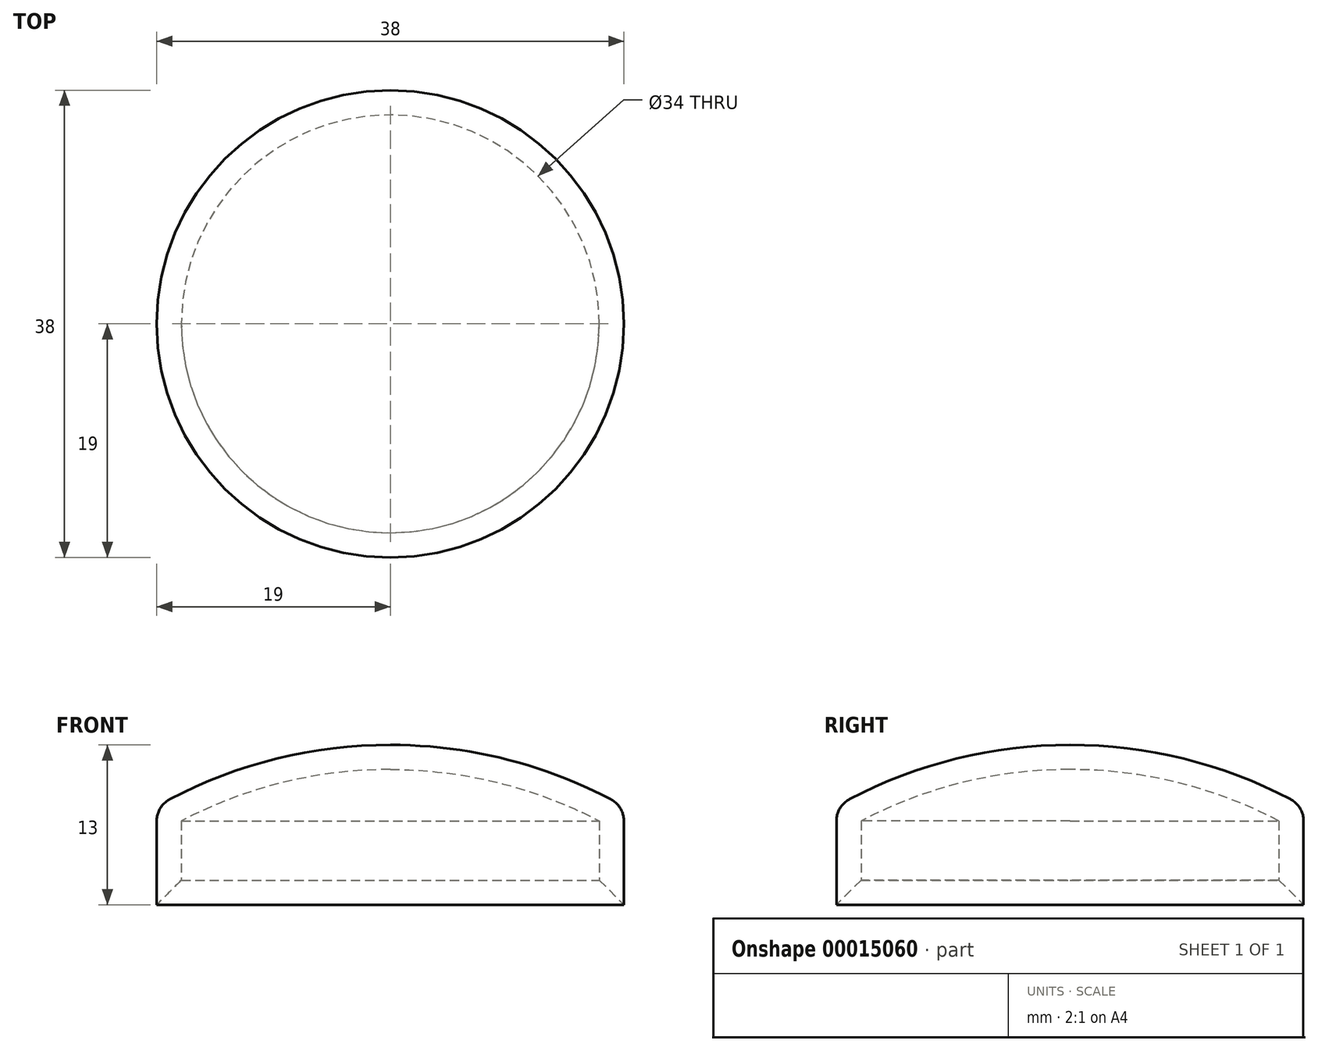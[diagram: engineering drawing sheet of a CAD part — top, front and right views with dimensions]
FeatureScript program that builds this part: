
annotation { "Feature Type Name" : "Feature", "Feature Type Description" : "" }
export const myFeature = defineFeature(function(context is Context, id is Id, definition is map)
    precondition{}
    {
        {
            var Q0;
            Q0=qCreatedBy(makeId("Front.planeOp"),FACE);
            var sketch = newSketch(context, id + "F0", { "sketchPlane" : qUnion([Q0])});
            skLineSegment(sketch, "E0", {"start": v(0, 0) * mm, "end": v(0, 25.64) * mm, "construction": true});
            skLineSegment(sketch, "E1", {"start": v(0, 0) * mm, "end": v(23.76, 0) * mm, "construction": true});
            skLineSegment(sketch, "E2.bottom", {"start": v(0, 0) * mm, "end": v(19, 0) * mm});
            skLineSegment(sketch, "E2.top", {"start": v(0, 8) * mm, "end": v(19, 8) * mm, "construction": true});
            skLineSegment(sketch, "E2.left", {"start": v(0, 0) * mm, "end": v(0, 8) * mm});
            skLineSegment(sketch, "E2.right", {"start": v(19, 0) * mm, "end": v(19, 6.81) * mm});
            skLineSegment(sketch, "E3.top", {"start": v(0, 13) * mm, "end": v(19, 13) * mm, "construction": true});
            skLineSegment(sketch, "E3.left", {"start": v(0, 8) * mm, "end": v(0, 13) * mm});
            skLineSegment(sketch, "E3.right", {"start": v(19, 8) * mm, "end": v(19, 13) * mm, "construction": true});
            skLineSegment(sketch, "E4.0.MirrorCS", {"start": v(0, 13) * mm, "end": v(-19, 13) * mm, "construction": true});
            skLineSegment(sketch, "E5.0.MirrorCS", {"start": v(-19, 8) * mm, "end": v(-19, 13) * mm, "construction": true});
            skLineSegment(sketch, "E6.0.MirrorCS", {"start": v(-19, 0) * mm, "end": v(-19, 8) * mm});
            skLineSegment(sketch, "E7.0.MirrorCS", {"start": v(0, 0) * mm, "end": v(-19, 0) * mm});
            skLineSegment(sketch, "E8.0.MirrorCS", {"start": v(0, 8) * mm, "end": v(-19, 8) * mm, "construction": true});
            skArc(sketch, "E9", {"start": v(17.93, 8.58) * mm, "mid": v(-0.6, 13) * mm, "end": v(-19, 8) * mm});
            skPoint(sketch, "E10.visualSharp", {"position": v(19, 8) * mm});
            skArc(sketch, "E10.filletArc", {"start": v(19, 6.81) * mm, "mid": v(18.71, 7.85) * mm, "end": v(17.93, 8.58) * mm});
            skArc(sketch, "E11.0", {"start": v(17, 6.81) * mm, "mid": v(-0.58, 11) * mm, "end": v(-18.02, 6.26) * mm});
            skLineSegment(sketch, "E11.1", {"start": v(17, 0) * mm, "end": v(17, 6.81) * mm});
            skSolve(sketch);
        }
        {
            var Q0;
            {var subQ7=sQuery(id+"F0.wireOp",EDGE,"E2.right");Q0=makeQuery(id+"F0.imprint","IMPRINT",FACE,{"disambiguationData":[TD([[makeQuery(id+"F0.imprint","IMPRINT",EDGE,{"derivedFrom":subQ7}),1.0]])]});}
            var Q1;
            Q1=sQuery(id+"F0.wireOp",EDGE,"E0");
            revolve(context, id + "F1", {"entities" : qUnion([Q0]), "axis" : qUnion([Q1]), "revolveType" : RevolveType.FULL});
        }
        {
            var Q0;
            Q0=makeQuery(id+"F1.opRevolve","SWEPT_EDGE",EDGE,{"disambiguationData":[OSD([sQuery(id+"F0.wireOp",EDGE,"E2.bottom"),sQuery(id+"F0.wireOp",EDGE,"E11.1")])]});
            chamfer(context, id + "F2", {"entities" : qUnion([Q0]), "width" : 2 * mm, "tangentPropagation" : true});
        }
    });
